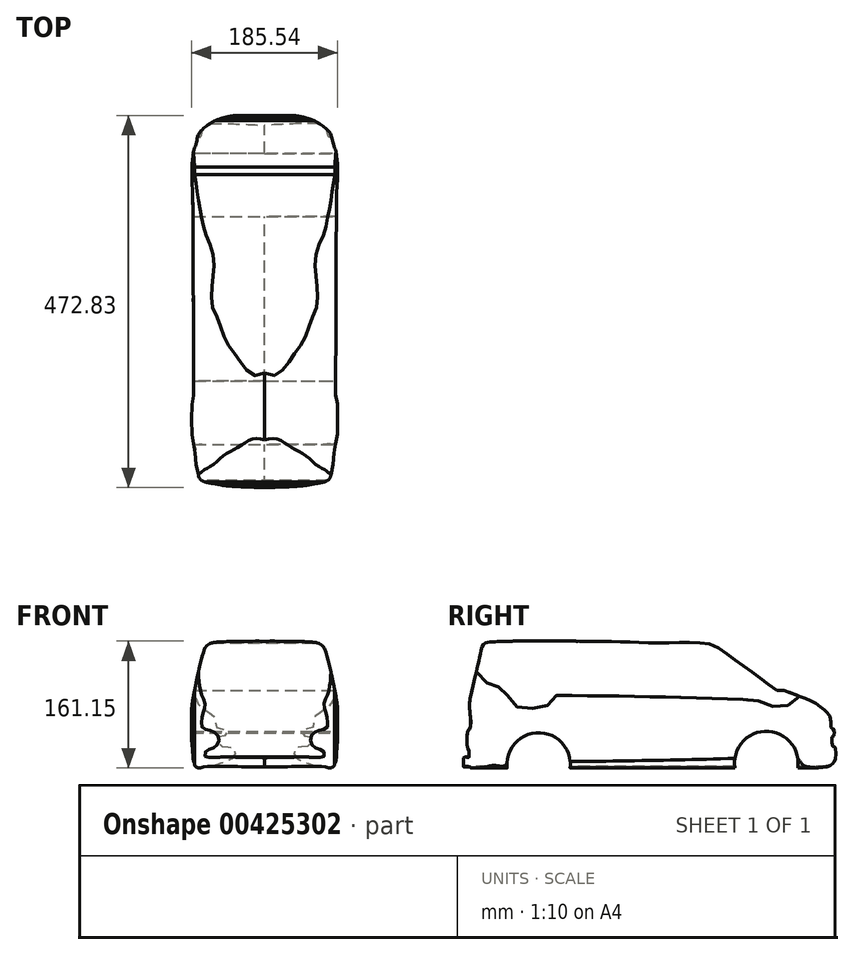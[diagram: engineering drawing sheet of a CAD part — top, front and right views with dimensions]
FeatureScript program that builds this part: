
annotation { "Feature Type Name" : "Feature", "Feature Type Description" : "" }
export const myFeature = defineFeature(function(context is Context, id is Id, definition is map)
    precondition{}
    {
        {
            var Q0;
            Q0=qCreatedBy(makeId("Front.planeOp"),FACE);
            var sketch = newSketch(context, id + "F0", { "sketchPlane" : qUnion([Q0])});
            skLineSegment(sketch, "E0", {"start": v(-100.12, 2.45) * mm, "end": v(90.28, 2.45) * mm, "construction": true});
            skLineSegment(sketch, "E1", {"start": v(90.28, 2.45) * mm, "end": v(90.28, 199.45) * mm, "construction": true});
            skLineSegment(sketch, "E2", {"start": v(-4.92, 190) * mm, "end": v(-4.92, -11.4) * mm});
            skPoint(sketch, "E2.startSnap0", {"position": v(-4.92, 2.45) * mm});
            skFitSpline(sketch, "E3", {"points": [v(-4.92, 186.13) * mm, v(-43.92, 185.82) * mm, v(-72.5, 183.82) * mm, v(-77.36, 181.24) * mm, v(-80.8, 176.96) * mm, v(-93.65, 125.23) * mm, v(-97.9, 98.43) * mm, v(-98.91, 78.72) * mm, v(-97.9, 53.23) * mm, v(-94.15, 29.44) * mm, v(-92.12, 26.72) * mm, v(-87.7, 25.02) * mm, v(-82.94, 26.04) * mm, v(-78.86, 26.72) * mm, v(-4.92, 26.38) * mm], "startDerivative": vector(-509.55, 3.47) * mm, "endDerivative": vector(680.88, -8.8) * mm});
            skFitSpline(sketch, "E4.MirrorCS", {"points": [v(-4.92, 186.13) * mm, v(34.1, 185.82) * mm, v(62.67, 183.82) * mm, v(67.53, 181.24) * mm, v(70.96, 176.96) * mm, v(83.82, 125.23) * mm, v(88.06, 98.43) * mm, v(89.08, 78.72) * mm, v(88.06, 53.23) * mm, v(84.32, 29.44) * mm, v(82.28, 26.72) * mm, v(77.86, 25.02) * mm, v(73.1, 26.04) * mm, v(69.03, 26.72) * mm, v(-4.92, 26.38) * mm], "startDerivative": vector(509.55, 3.47) * mm, "endDerivative": vector(-680.88, -8.8) * mm});
            skSolve(sketch);
        }
        {
            var Q0;
            {var subQ1=sQuery(id+"F0.wireOp",EDGE,"E3");Q0=makeQuery(id+"F0.imprint","IMPRINT",FACE,{"disambiguationData":[TD([[makeQuery(id+"F0.imprint","IMPRINT",EDGE,{"derivedFrom":subQ1}),1.0]])]});}
            var Q1;
            {var subQ0=sQuery(id+"F0.wireOp",EDGE,"E4.MirrorCS");Q1=makeQuery(id+"F0.imprint","IMPRINT",FACE,{"disambiguationData":[TD([[makeQuery(id+"F0.imprint","IMPRINT",EDGE,{"derivedFrom":subQ0}),-1.0]])]});}
            extrude(context, id + "F1", {"entities" : qUnion([Q0, Q1]), "depth" : 489.2 * mm});
        }
        {
            var Q0;
            Q0=qCreatedBy(makeId("Right.planeOp"),FACE);
            var sketch = newSketch(context, id + "F2", { "sketchPlane" : qUnion([Q0])});
            skFitSpline(sketch, "E5", {"points": [v(-50.94, 24.1) * mm, v(-129.36, 21.28) * mm, v(-341.15, 23.7) * mm, v(-420.46, 24.83) * mm, v(-472.8, 25.51) * mm, v(-476.2, 27.55) * mm, v(-476.54, 34.69) * mm, v(-474.16, 38.77) * mm, v(-468.39, 38.77) * mm, v(-468.39, 41.49) * mm, v(-468.39, 46.93) * mm, v(-470.09, 49.98) * mm, v(-470.09, 71.4) * mm, v(-466.69, 76.5) * mm, v(-467.81, 99.65) * mm, v(-467.81, 111.2) * mm, v(-465.77, 120.04) * mm, v(-453.2, 173.74) * mm, v(-451.16, 180.54) * mm, v(-449.12, 182.58) * mm, v(-444.7, 184.62) * mm, v(-265.28, 185.18) * mm, v(-258.79, 184.94) * mm, v(-247.25, 184.22) * mm, v(-223.94, 183.98) * mm, v(-183.8, 184.46) * mm, v(-164.62, 182.82) * mm, v(-158.96, 181) * mm, v(-151.48, 177.16) * mm, v(-77.58, 123.48) * mm], "startDerivative": vector(-991.54, -57.36) * mm, "endDerivative": vector(1328.54, -992.84) * mm});
            skLineSegment(sketch, "E6", {"start": v(-77.58, 123.48) * mm, "end": v(-68.21, 123.48) * mm});
            skFitSpline(sketch, "E7", {"points": [v(-68.21, 123.48) * mm, v(-33.84, 110.26) * mm, v(-26.63, 106.18) * mm, v(-19.18, 100.65) * mm, v(-15.58, 96.8) * mm, v(-14.62, 95.36) * mm, v(-12.7, 94.64) * mm, v(-10.77, 92.48) * mm, v(-8.85, 87.67) * mm, v(-9.1, 83.1) * mm, v(-9.1, 78.06) * mm, v(-9.06, 77.05) * mm, v(-6.63, 75.33) * mm, v(-4.91, 73.05) * mm, v(-4.2, 70.62) * mm, v(-4.48, 67.19) * mm, v(-4.91, 66.04) * mm, v(-6.34, 65.04) * mm, v(-7.49, 64.19) * mm, v(-7.77, 62.33) * mm, v(-7.63, 54.18) * mm, v(-6.77, 53.04) * mm, v(-4.91, 52.18) * mm, v(-3.34, 51.33) * mm, v(-2.63, 48.61) * mm, v(-3.14, 37.26) * mm, v(-4.5, 33.7) * mm, v(-8.06, 29.28) * mm, v(-15.2, 26.39) * mm, v(-28.63, 25.2) * mm, v(-36.78, 24.18) * mm, v(-50.94, 24.1) * mm], "startDerivative": vector(458.74, -167.78) * mm, "endDerivative": vector(-277.84, 6.41) * mm});
            skLineSegment(sketch, "E8.bottom", {"start": v(-504.65, 215.9) * mm, "end": v(47.52, 215.9) * mm});
            skLineSegment(sketch, "E8.top", {"start": v(-504.65, -25.33) * mm, "end": v(47.52, -25.33) * mm});
            skLineSegment(sketch, "E8.left", {"start": v(-504.65, 215.9) * mm, "end": v(-504.65, -25.33) * mm});
            skLineSegment(sketch, "E8.right", {"start": v(47.52, 215.9) * mm, "end": v(47.52, -25.33) * mm});
            skSolve(sketch);
        }
        {
            var Q0;
            Q0=makeQuery(id+"F2.imprint","IMPRINT",FACE,{"disambiguationData":[TD([[makeQuery(id+"F2.imprint","IMPRINT",EDGE,{"derivedFrom":sQuery(id+"F2.wireOp",EDGE,"E5")}),1.0]])]});
            var Q1;
            Q1=sQuery(id+"F2.wireOp",EDGE,"E5");
            var Q2;
            Q2=sQuery(id+"F2.wireOp",EDGE,"E7");
            extrude(context, id + "F3", {"entities" : qUnion([Q0]), "operationType" : NewBodyOperationType.REMOVE, "surfaceEntities" : qUnion([Q1, Q2]), "endBound" : BoundingType.SYMMETRIC, "oppositeDirection" : true, "depth" : 300 * mm});
        }
        {
            var Q0;
            Q0=qCreatedBy(makeId("Top.planeOp"),FACE);
            var sketch = newSketch(context, id + "F4", { "sketchPlane" : qUnion([Q0])});
            skLineSegment(sketch, "E9", {"start": v(-4.96, 45.44) * mm, "end": v(-4.96, -480.26) * mm, "construction": true});
            skFitSpline(sketch, "E10", {"points": [v(-4.96, -475.4) * mm, v(-28.13, -474.44) * mm, v(-53.6, -473) * mm, v(-67.3, -470.6) * mm, v(-81.96, -467.7) * mm, v(-87.25, -464.1) * mm, v(-89.17, -459.3) * mm, v(-90.61, -450.88) * mm, v(-92.53, -444.64) * mm, v(-93.74, -436.95) * mm, v(-93.06, -424.58) * mm, v(-95.63, -418.87) * mm, v(-97.06, -412) * mm, v(-97.63, -404) * mm, v(-97.35, -370.28) * mm, v(-96.78, -366.85) * mm, v(-95.63, -364) * mm, v(-95.23, -358.76) * mm, v(-96.33, -105.47) * mm, v(-96.67, -98.68) * mm, v(-97.52, -76.75) * mm, v(-96.67, -55.86) * mm, v(-94.85, -46.57) * mm, v(-92.43, -40.1) * mm, v(-90, -29.8) * mm, v(-87.98, -24.74) * mm, v(-83.13, -19.49) * mm, v(-67.16, -8.98) * mm, v(-35.23, -1.7) * mm, v(-4.96, 0) * mm], "startDerivative": vector(-514.08, 23.05) * mm, "endDerivative": vector(595.73, 17.4) * mm});
            skFitSpline(sketch, "E11.MirrorCS", {"points": [v(-4.96, -475.4) * mm, v(18.21, -474.44) * mm, v(43.69, -473) * mm, v(57.38, -470.6) * mm, v(72.04, -467.7) * mm, v(77.33, -464.1) * mm, v(79.25, -459.3) * mm, v(80.7, -450.88) * mm, v(82.62, -444.64) * mm, v(83.82, -436.95) * mm, v(83.15, -424.58) * mm, v(85.72, -418.87) * mm, v(87.15, -412) * mm, v(87.72, -404) * mm, v(87.43, -370.28) * mm, v(86.86, -366.85) * mm, v(85.72, -364) * mm, v(85.31, -358.76) * mm, v(86.41, -105.47) * mm, v(86.75, -98.68) * mm, v(87.6, -76.75) * mm, v(86.76, -55.86) * mm, v(84.94, -46.57) * mm, v(82.51, -40.1) * mm, v(80.09, -29.8) * mm, v(78.07, -24.74) * mm, v(73.22, -19.49) * mm, v(57.25, -8.98) * mm, v(25.32, -1.7) * mm, v(-4.96, 0) * mm], "startDerivative": vector(514.08, 23.05) * mm, "endDerivative": vector(-595.73, 17.4) * mm});
            skLineSegment(sketch, "E12.bottom", {"start": v(-133.05, -508.34) * mm, "end": v(120.78, -508.34) * mm});
            skLineSegment(sketch, "E12.top", {"start": v(-133.05, 49.44) * mm, "end": v(120.78, 49.44) * mm});
            skLineSegment(sketch, "E12.left", {"start": v(-133.05, -508.34) * mm, "end": v(-133.05, 49.44) * mm});
            skLineSegment(sketch, "E12.right", {"start": v(120.78, -508.34) * mm, "end": v(120.78, 49.44) * mm});
            skSolve(sketch);
        }
        {
            var Q0;
            Q0 = qSketchRegion(id + "F4", true);
            extrude(context, id + "F5", {"entities" : qUnion([Q0]), "operationType" : NewBodyOperationType.REMOVE, "depth" : 195 * mm});
        }
        {
            var Q0;
            Q0=makeQuery(id+"F2.imprint","IMPRINT",FACE,{"disambiguationData":[TD([[makeQuery(id+"F2.imprint","IMPRINT",EDGE,{"derivedFrom":sQuery(id+"F2.wireOp",EDGE,"E5")}),1.0]])]});
            var sketch = newSketch(context, id + "F6", { "sketchPlane" : qUnion([Q0])});
            skLineSegment(sketch, "E13", {"start": v(-420.09, 24.74) * mm, "end": v(-340.39, 23.21) * mm});
            skArc(sketch, "E14", {"start": v(-340.39, 23.21) * mm, "mid": v(-379.36, 69.94) * mm, "end": v(-420.09, 24.74) * mm});
            skArc(sketch, "E15", {"start": v(-51.1, 23.98) * mm, "mid": v(-92.32, 71.73) * mm, "end": v(-129.9, 21.07) * mm});
            skLineSegment(sketch, "E16", {"start": v(-129.9, 21.07) * mm, "end": v(-51.1, 23.98) * mm});
            skSolve(sketch);
        }
        {
            var Q0;
            Q0 = qSketchRegion(id + "F6", true);
            extrude(context, id + "F7", {"entities" : qUnion([Q0]), "operationType" : NewBodyOperationType.REMOVE, "endBound" : BoundingType.SYMMETRIC, "oppositeDirection" : true, "depth" : 256 * mm});
        }
    });
